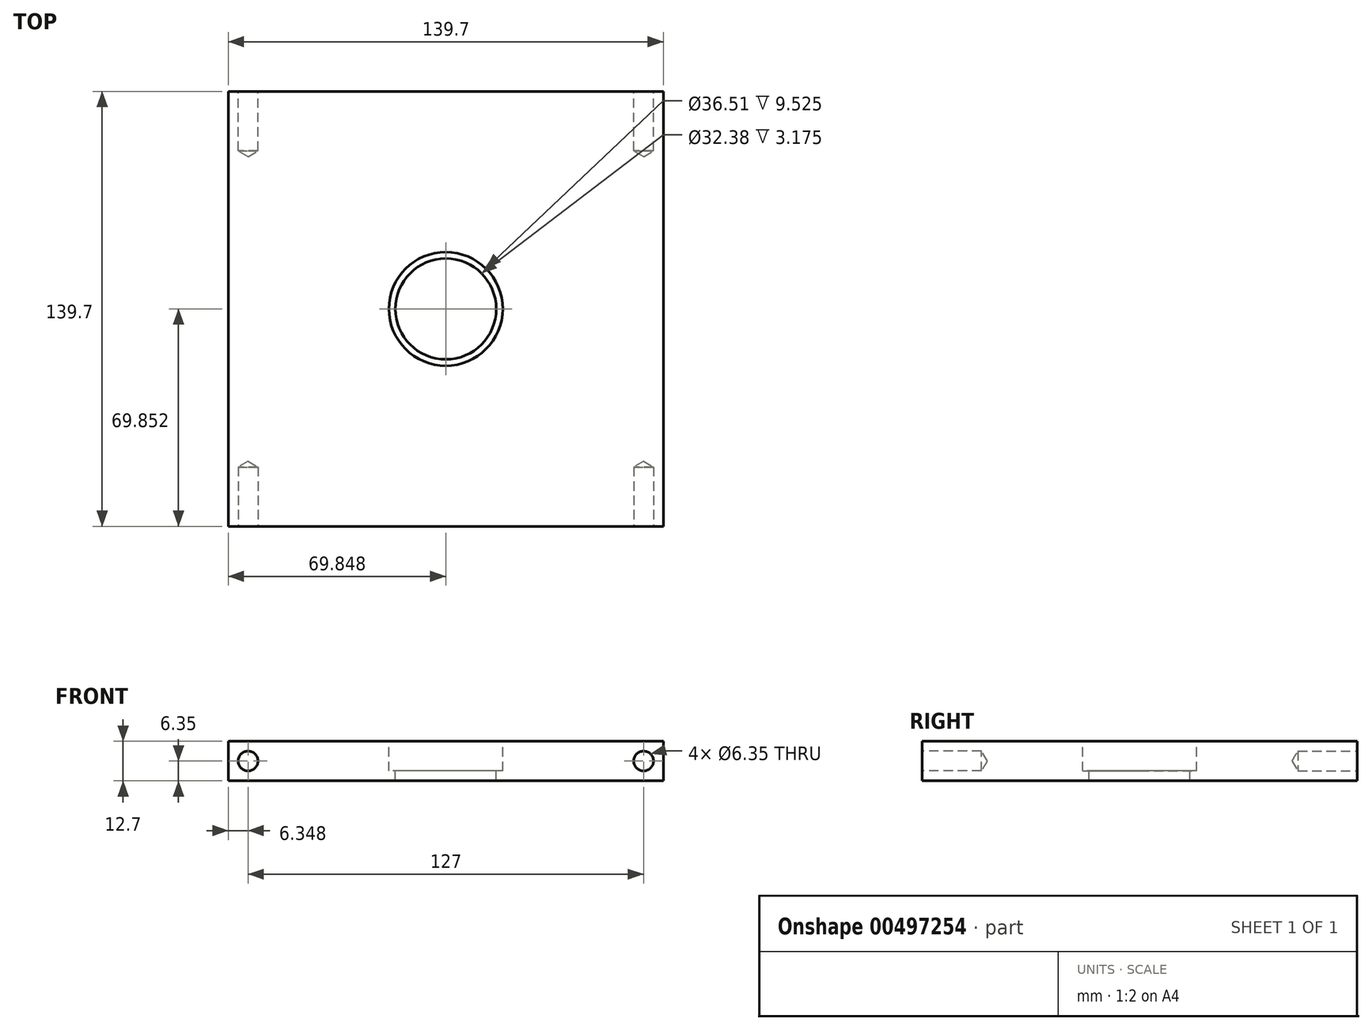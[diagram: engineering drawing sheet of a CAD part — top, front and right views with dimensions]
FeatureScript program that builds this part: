
annotation { "Feature Type Name" : "Feature", "Feature Type Description" : "" }
export const myFeature = defineFeature(function(context is Context, id is Id, definition is map)
    precondition{}
    {
        {
            var Q0;
            Q0=qCreatedBy(makeId("Top.planeOp"),FACE);
            var sketch = newSketch(context, id + "F0", { "sketchPlane" : qUnion([Q0])});
            skLineSegment(sketch, "E0.bottom", {"start": v(-62.36, 81.41) * mm, "end": v(77.34, 81.41) * mm});
            skLineSegment(sketch, "E0.top", {"start": v(-62.36, -58.29) * mm, "end": v(77.34, -58.29) * mm});
            skLineSegment(sketch, "E0.left", {"start": v(-62.36, 81.41) * mm, "end": v(-62.36, -58.29) * mm});
            skLineSegment(sketch, "E0.right", {"start": v(77.34, 81.41) * mm, "end": v(77.34, -58.29) * mm});
            skSolve(sketch);
        }
        {
            var Q0;
            Q0=makeQuery(id+"F0.imprint","IMPRINT",FACE,{"disambiguationData":[TD([[makeQuery(id+"F0.imprint","IMPRINT",EDGE,{"derivedFrom":sQuery(id+"F0.wireOp",EDGE,"E0.bottom")}),-1.0]])]});
            extrude(context, id + "F1", {"entities" : qUnion([Q0]), "depth" : 12.7 * mm});
        }
        {
            var Q0;
            Q0=makeQuery(id+"F1.opExtrude","CAP_FACE",FACE,{"disambiguationData":[OSD([sQuery(id+"F0.wireOp",EDGE,"E0.bottom"),sQuery(id+"F0.wireOp",EDGE,"E0.top"),sQuery(id+"F0.wireOp",EDGE,"E0.left"),sQuery(id+"F0.wireOp",EDGE,"E0.right")])],"isStart":false});
            var sketch = newSketch(context, id + "F2", { "sketchPlane" : qUnion([Q0])});
            skCircle(sketch, "E1", {"center": v(7.49, 11.56) * mm, "radius": 18.26 * mm});
            skPoint(sketch, "E1.centerSnap0", {"position": v(-62.36, 11.56) * mm});
            skPoint(sketch, "E1.centerSnap1", {"position": v(7.49, 81.41) * mm});
            skCircle(sketch, "E2", {"center": v(7.49, 11.56) * mm, "radius": 16.2 * mm});
            skSolve(sketch);
        }
        {
            var Q0;
            Q0 = qSketchRegion(id + "F2", true);
            extrude(context, id + "F3", {"entities" : qUnion([Q0]), "operationType" : NewBodyOperationType.REMOVE, "oppositeDirection" : true, "depth" : 9.52 * mm});
        }
        {
            var Q0;
            Q0=makeQuery(id+"F3.boolean.opBoolean","SPLIT",FACE,{"disambiguationData":[TD([makeQuery(id+"F3.opExtrude","SWEPT_FACE",FACE,{"disambiguationData":[OSD([sQuery(id+"F2.wireOp",EDGE,"E2")])]})])],"derivedFrom":makeQuery(id+"F1.opExtrude","CAP_FACE",FACE,{"disambiguationData":[OSD([sQuery(id+"F0.wireOp",EDGE,"E0.bottom"),sQuery(id+"F0.wireOp",EDGE,"E0.top"),sQuery(id+"F0.wireOp",EDGE,"E0.left"),sQuery(id+"F0.wireOp",EDGE,"E0.right")])],"isStart":false})});
            extrude(context, id + "F4", {"entities" : qUnion([Q0]), "operationType" : NewBodyOperationType.REMOVE, "oppositeDirection" : true, "depth" : 25.4 * mm, "offsetDistance" : 25.4 * mm});
        }
        {
            var Q0;
            Q0=makeQuery(id+"F1.opExtrude","SWEPT_FACE",FACE,{"disambiguationData":[OSD([sQuery(id+"F0.wireOp",EDGE,"E0.top")])]});
            var sketch = newSketch(context, id + "F5", { "sketchPlane" : qUnion([Q0])});
            skPoint(sketch, "E3", {"position": v(-56.01, 6.35) * mm});
            skPoint(sketch, "E4", {"position": v(70.99, 6.35) * mm});
            skSolve(sketch);
        }
        {
            var Q0;
            Q0=makeQuery(id+"F1.opExtrude","SWEPT_FACE",FACE,{"disambiguationData":[OSD([sQuery(id+"F0.wireOp",EDGE,"E0.bottom")])]});
            var sketch = newSketch(context, id + "F6", { "sketchPlane" : qUnion([Q0])});
            skPoint(sketch, "E5", {"position": v(-70.99, 6.35) * mm});
            skPoint(sketch, "E6", {"position": v(56.01, 6.35) * mm});
            skSolve(sketch);
        }
        {
            var Q0;
            Q0=sQuery(id+"F5.wireOp",VERTEX,"E3");
            var Q1;
            Q1=sQuery(id+"F5.wireOp",VERTEX,"E4");
            var Q2;
            Q2=sQuery(id+"F6.wireOp",VERTEX,"E5");
            var Q3;
            Q3=sQuery(id+"F6.wireOp",VERTEX,"E6");
            var Q4;
            Q4=makeQuery(id+"F1.opExtrude","SWEPT_BODY",BODY,{"disambiguationData":[OSD([sQuery(id+"F0.wireOp",EDGE,"E0.bottom"),sQuery(id+"F0.wireOp",EDGE,"E0.top"),sQuery(id+"F0.wireOp",EDGE,"E0.left"),sQuery(id+"F0.wireOp",EDGE,"E0.right")])]});
            hole(context, id + "F7", {"style" : HoleStyle.SIMPLE, "endStyle" : HoleEndStyle.BLIND, "holeDiameter" : 6.35 * mm, "holeDepth" : 19.05 * mm, "isTappedThrough" : true, "tappedDepth" : 12.7 * mm, "tapClearance" : 3, "startFromSketch" : true, "locations" : qUnion([Q0, Q1, Q2, Q3]), "scope" : qUnion([Q4])});
        }
    });
